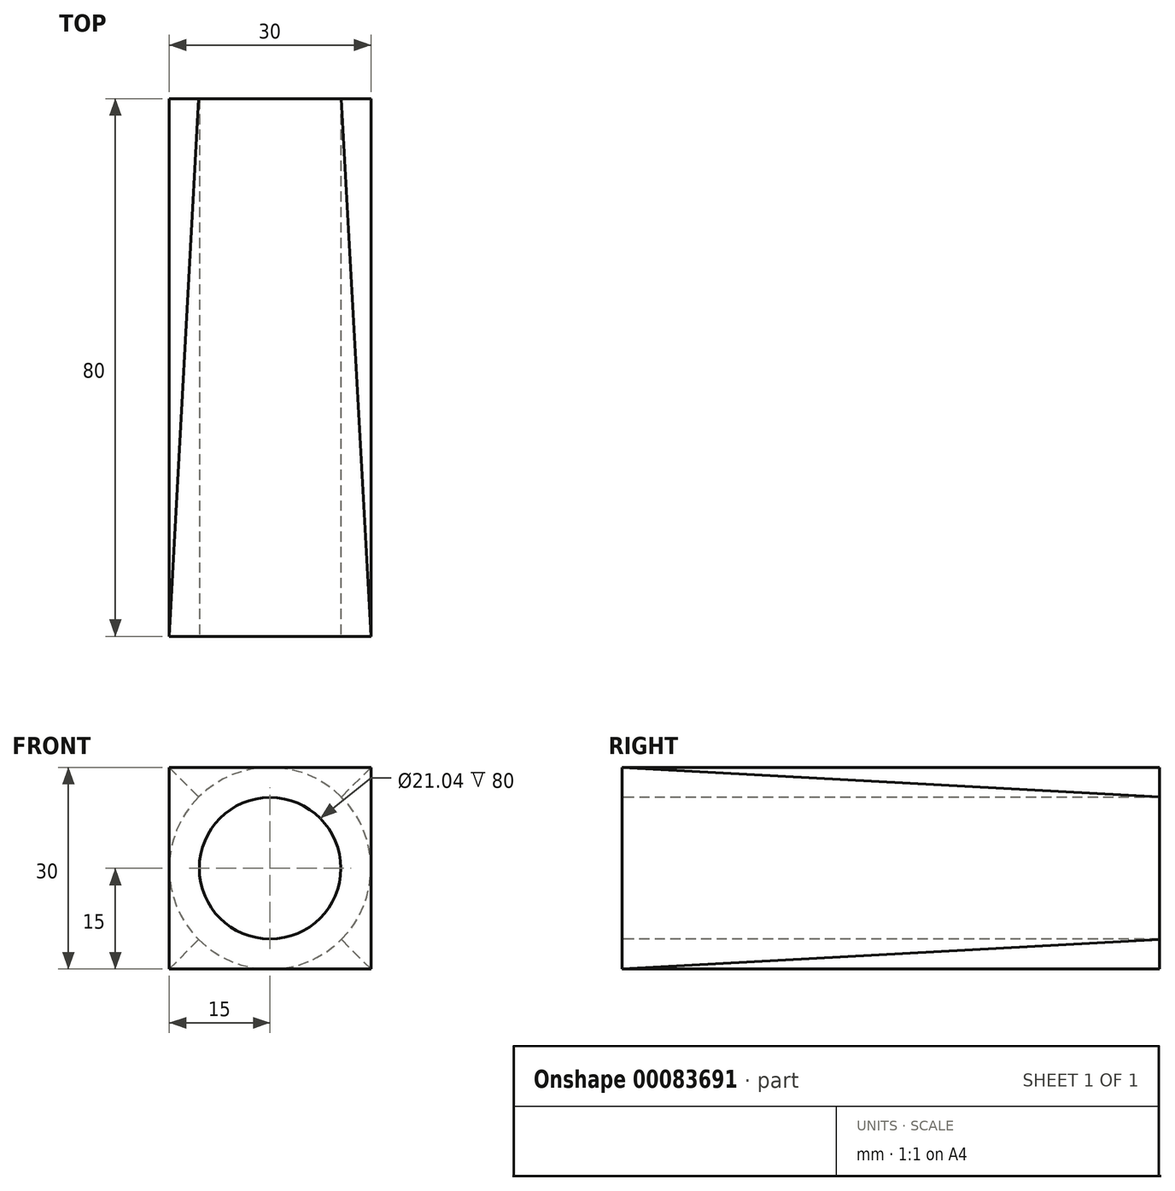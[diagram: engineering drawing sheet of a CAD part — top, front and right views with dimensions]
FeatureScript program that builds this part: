
annotation { "Feature Type Name" : "Feature", "Feature Type Description" : "" }
export const myFeature = defineFeature(function(context is Context, id is Id, definition is map)
    precondition{}
    {
        {
            var Q0;
            Q0=qCreatedBy(makeId("Front.planeOp"),FACE);
            var sketch = newSketch(context, id + "F0", { "sketchPlane" : qUnion([Q0])});
            skCircle(sketch, "E0", {"center": v(0, 0) * mm, "radius": 15 * mm});
            skSolve(sketch);
        }
        {
            var Q0;
            Q0=qCreatedBy(makeId("Front.planeOp"),FACE);
            cPlane(context, id + "F1", {"entities" : qUnion([Q0]), "cplaneType" : CPlaneType.OFFSET, "offset" : 80 * mm, "width" : 150 * mm, "height" : 150 * mm});
        }
        {
            var Q0;
            Q0=qCreatedBy(id+"F1.planeOp",FACE);
            var sketch = newSketch(context, id + "F2", { "sketchPlane" : qUnion([Q0])});
            skLineSegment(sketch, "E1.bottom", {"start": v(15, -15) * mm, "end": v(-15, -15) * mm});
            skLineSegment(sketch, "E1.top", {"start": v(15, 15) * mm, "end": v(-15, 15) * mm});
            skLineSegment(sketch, "E1.left", {"start": v(15, -15) * mm, "end": v(15, 15) * mm});
            skLineSegment(sketch, "E1.right", {"start": v(-15, -15) * mm, "end": v(-15, 15) * mm});
            skPoint(sketch, "E1.middle", {"position": v(0, 0) * mm});
            skSolve(sketch);
        }
        {
            var Q0;
            Q0=makeQuery(id+"F2.imprint","IMPRINT",FACE,{"disambiguationData":[TD([[makeQuery(id+"F2.imprint","IMPRINT",EDGE,{"derivedFrom":sQuery(id+"F2.wireOp",EDGE,"E1.bottom")}),-1.0]])]});
            var Q1;
            Q1=makeQuery(id+"F0.imprint","IMPRINT",FACE,{"disambiguationData":[TD([[makeQuery(id+"F0.imprint","IMPRINT",EDGE,{"derivedFrom":sQuery(id+"F0.wireOp",EDGE,"E0")}),1.0]])]});
            loft(context, id + "F3", {"sheetProfilesArray" : [{ "sheetProfileEntities" : qUnion([Q0]) }, { "sheetProfileEntities" : qUnion([Q1]) }]});
        }
        {
            var Q0;
            Q0=qCreatedBy(id+"F1.planeOp",FACE);
            var sketch = newSketch(context, id + "F4", { "sketchPlane" : qUnion([Q0])});
            skCircle(sketch, "E2", {"center": v(0, 0) * mm, "radius": 10.52 * mm});
            skSolve(sketch);
        }
        {
            var Q0;
            Q0=makeQuery(id+"F4.imprint","IMPRINT",FACE,{"disambiguationData":[TD([[makeQuery(id+"F4.imprint","IMPRINT",EDGE,{"derivedFrom":sQuery(id+"F4.wireOp",EDGE,"E2")}),1.0]])]});
            extrude(context, id + "F5", {"entities" : qUnion([Q0]), "operationType" : NewBodyOperationType.REMOVE, "endBound" : BoundingType.THROUGH_ALL, "oppositeDirection" : true, "depth" : 25 * mm});
        }
    });
